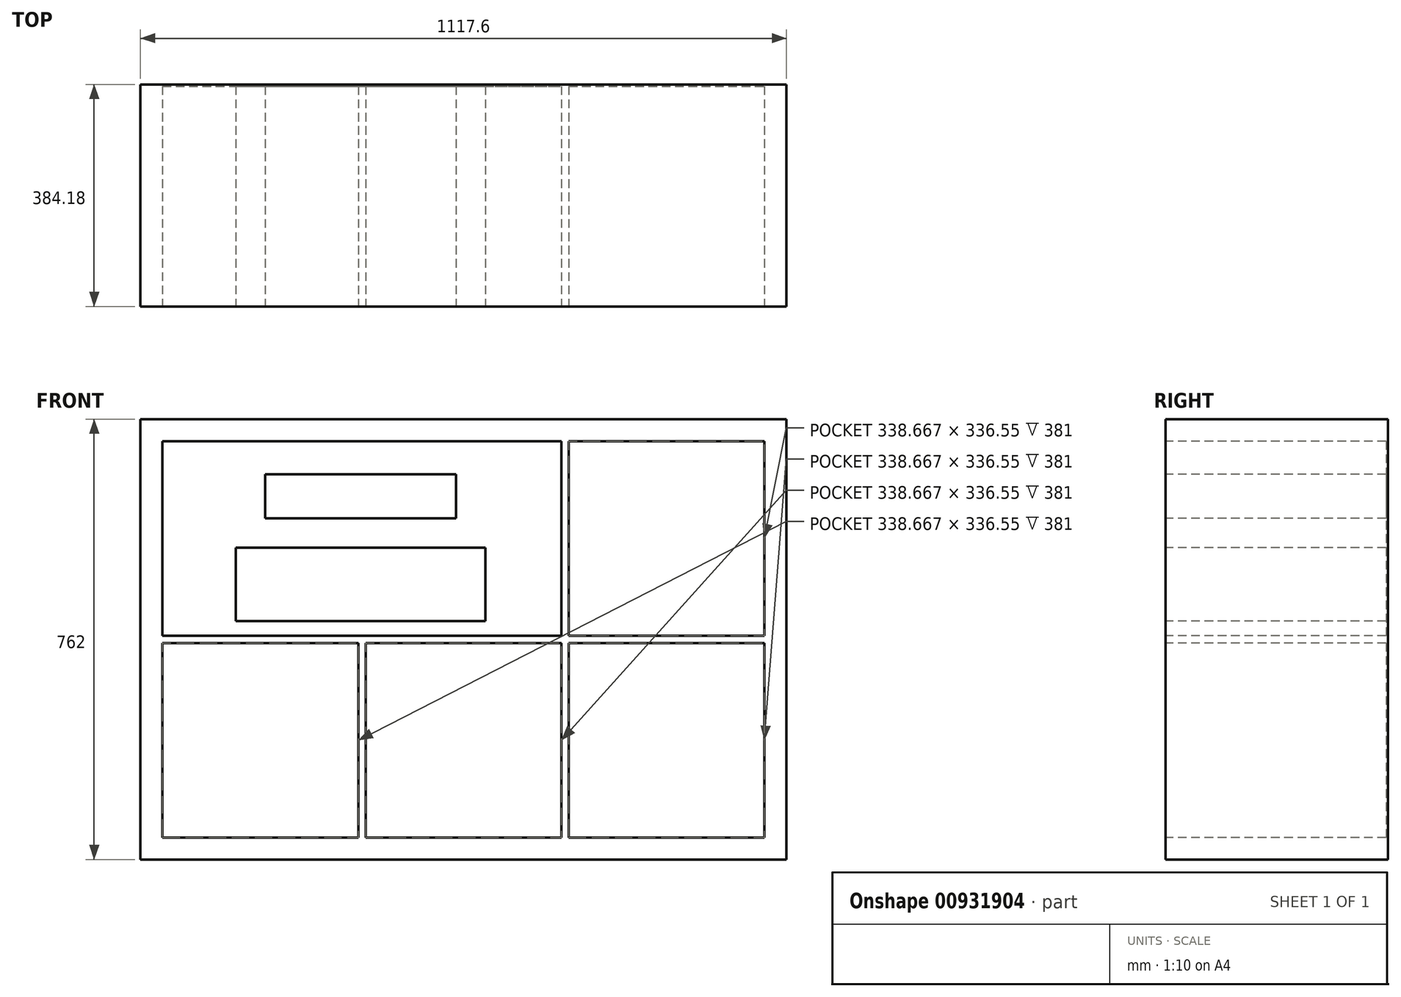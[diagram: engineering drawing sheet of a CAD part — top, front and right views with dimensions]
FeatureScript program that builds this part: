
annotation { "Feature Type Name" : "Feature", "Feature Type Description" : "" }
export const myFeature = defineFeature(function(context is Context, id is Id, definition is map)
    precondition{}
    {
        {
            var Q0;
            Q0=qCreatedBy(makeId("Front.planeOp"),FACE);
            var sketch = newSketch(context, id + "F0", { "sketchPlane" : qUnion([Q0])});
            skLineSegment(sketch, "E0.bottom", {"start": v(0, 0) * mm, "end": v(1117.6, 0) * mm});
            skLineSegment(sketch, "E0.top", {"start": v(0, -762) * mm, "end": v(1117.6, -762) * mm});
            skLineSegment(sketch, "E0.left", {"start": v(0, 0) * mm, "end": v(0, -762) * mm});
            skLineSegment(sketch, "E0.right", {"start": v(1117.6, 0) * mm, "end": v(1117.6, -762) * mm});
            skLineSegment(sketch, "E1.0", {"start": v(38.1, -38.1) * mm, "end": v(376.77, -38.1) * mm});
            skLineSegment(sketch, "E1.1", {"start": v(38.1, -38.1) * mm, "end": v(38.1, -374.65) * mm});
            skLineSegment(sketch, "E1.2", {"start": v(38.1, -723.9) * mm, "end": v(376.77, -723.9) * mm});
            skLineSegment(sketch, "E1.3", {"start": v(1079.5, -38.1) * mm, "end": v(1079.5, -374.65) * mm});
            skLineSegment(sketch, "E2", {"start": v(376.77, -374.65) * mm, "end": v(38.1, -374.65) * mm});
            skLineSegment(sketch, "E3", {"start": v(38.1, -387.35) * mm, "end": v(376.77, -387.35) * mm});
            skLineSegment(sketch, "E4", {"start": v(376.77, -387.35) * mm, "end": v(376.77, -723.9) * mm});
            skLineSegment(sketch, "E5", {"start": v(389.47, -374.65) * mm, "end": v(728.13, -374.65) * mm});
            skLineSegment(sketch, "E6", {"start": v(389.47, -723.9) * mm, "end": v(389.47, -387.35) * mm});
            skLineSegment(sketch, "E7", {"start": v(389.47, -387.35) * mm, "end": v(728.13, -387.35) * mm});
            skLineSegment(sketch, "E8.trimOffspring", {"start": v(38.1, -387.35) * mm, "end": v(38.1, -723.9) * mm});
            skLineSegment(sketch, "E9.trimOffspring", {"start": v(389.47, -38.1) * mm, "end": v(728.13, -38.1) * mm});
            skLineSegment(sketch, "E10.trimOffspring", {"start": v(1079.5, -387.35) * mm, "end": v(1079.5, -723.9) * mm});
            skLineSegment(sketch, "E11.trimOffspring", {"start": v(389.47, -723.9) * mm, "end": v(728.13, -723.9) * mm});
            skLineSegment(sketch, "E12", {"start": v(728.13, -38.1) * mm, "end": v(728.13, -374.65) * mm});
            skLineSegment(sketch, "E13", {"start": v(728.13, -387.35) * mm, "end": v(728.13, -723.9) * mm});
            skLineSegment(sketch, "E14", {"start": v(740.83, -38.1) * mm, "end": v(740.83, -374.65) * mm});
            skLineSegment(sketch, "E15", {"start": v(740.83, -387.35) * mm, "end": v(740.83, -723.9) * mm});
            skLineSegment(sketch, "E16.trimOffspring", {"start": v(740.83, -374.65) * mm, "end": v(1079.5, -374.65) * mm});
            skLineSegment(sketch, "E17.trimOffspring", {"start": v(740.83, -387.35) * mm, "end": v(1079.5, -387.35) * mm});
            skLineSegment(sketch, "E18.trimOffspring", {"start": v(740.83, -38.1) * mm, "end": v(1079.5, -38.1) * mm});
            skLineSegment(sketch, "E19.trimOffspring", {"start": v(740.83, -723.9) * mm, "end": v(1079.5, -723.9) * mm});
            skLineSegment(sketch, "E20", {"start": v(376.77, -38.1) * mm, "end": v(389.47, -38.1) * mm});
            skLineSegment(sketch, "E21", {"start": v(376.77, -374.65) * mm, "end": v(389.47, -374.65) * mm});
            skSolve(sketch);
        }
        {
            var Q0;
            Q0 = qSketchRegion(id + "F0", true);
            extrude(context, id + "F1", {"entities" : qUnion([Q0]), "oppositeDirection" : true, "depth" : 381 * mm, "offsetDistance" : 25.4 * mm});
        }
        {
            var Q0;
            Q0=makeQuery(id+"F1.opExtrude","CAP_FACE",FACE,{"disambiguationData":[OSD([sQuery(id+"F0.wireOp",EDGE,"E0.bottom"),sQuery(id+"F0.wireOp",EDGE,"E0.top"),sQuery(id+"F0.wireOp",EDGE,"E0.left"),sQuery(id+"F0.wireOp",EDGE,"E0.right"),sQuery(id+"F0.wireOp",EDGE,"E1.0"),sQuery(id+"F0.wireOp",EDGE,"E1.1"),sQuery(id+"F0.wireOp",EDGE,"E1.2"),sQuery(id+"F0.wireOp",EDGE,"E1.3"),sQuery(id+"F0.wireOp",EDGE,"unziumOY-lIAx-JzAN-9OzO-1yle08CG23bp"),sQuery(id+"F0.wireOp",EDGE,"E2"),sQuery(id+"F0.wireOp",EDGE,"E3"),sQuery(id+"F0.wireOp",EDGE,"E4"),sQuery(id+"F0.wireOp",EDGE,"X8ePQyhm-fYrp-kanb-HCO6-ofaEMRqhhf3u"),sQuery(id+"F0.wireOp",EDGE,"E5"),sQuery(id+"F0.wireOp",EDGE,"E6"),sQuery(id+"F0.wireOp",EDGE,"E7"),sQuery(id+"F0.wireOp",EDGE,"E8.trimOffspring"),sQuery(id+"F0.wireOp",EDGE,"E9.trimOffspring"),sQuery(id+"F0.wireOp",EDGE,"E10.trimOffspring"),sQuery(id+"F0.wireOp",EDGE,"E11.trimOffspring")])],"isStart":false});
            var sketch = newSketch(context, id + "F2", { "sketchPlane" : qUnion([Q0])});
            skLineSegment(sketch, "E22.bottom", {"start": v(-1117.6, 0) * mm, "end": v(0, 0) * mm});
            skLineSegment(sketch, "E22.top", {"start": v(-1117.6, -762) * mm, "end": v(0, -762) * mm});
            skLineSegment(sketch, "E22.left", {"start": v(-1117.6, 0) * mm, "end": v(-1117.6, -762) * mm});
            skLineSegment(sketch, "E22.right", {"start": v(0, 0) * mm, "end": v(0, -762) * mm});
            skSolve(sketch);
        }
        {
            var Q0;
            Q0 = qSketchRegion(id + "F2", true);
            extrude(context, id + "F3", {"entities" : qUnion([Q0]), "operationType" : NewBodyOperationType.ADD, "depth" : 3.17 * mm, "offsetDistance" : 25.4 * mm});
        }
        {
            var Q0;
            Q0=qCreatedBy(makeId("Front.planeOp"),FACE);
            var sketch = newSketch(context, id + "F4", { "sketchPlane" : qUnion([Q0])});
            skLineSegment(sketch, "E23.bottom", {"start": v(215.9, -95.25) * mm, "end": v(546.1, -95.25) * mm});
            skLineSegment(sketch, "E23.top", {"start": v(215.9, -171.45) * mm, "end": v(546.1, -171.45) * mm});
            skLineSegment(sketch, "E23.left", {"start": v(215.9, -95.25) * mm, "end": v(215.9, -171.45) * mm});
            skLineSegment(sketch, "E23.right", {"start": v(546.1, -95.25) * mm, "end": v(546.1, -171.45) * mm});
            skLineSegment(sketch, "E24.bottom", {"start": v(165.1, -222.25) * mm, "end": v(596.9, -222.25) * mm});
            skLineSegment(sketch, "E24.top", {"start": v(165.1, -349.25) * mm, "end": v(596.9, -349.25) * mm});
            skLineSegment(sketch, "E24.left", {"start": v(165.1, -222.25) * mm, "end": v(165.1, -349.25) * mm});
            skLineSegment(sketch, "E24.right", {"start": v(596.9, -222.25) * mm, "end": v(596.9, -349.25) * mm});
            skSolve(sketch);
        }
        {
            var Q0;
            Q0 = qSketchRegion(id + "F4", true);
            extrude(context, id + "F5", {"entities" : qUnion([Q0]), "operationType" : NewBodyOperationType.ADD, "oppositeDirection" : true, "depth" : 381 * mm, "offsetDistance" : 25.4 * mm});
        }
    });
